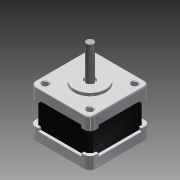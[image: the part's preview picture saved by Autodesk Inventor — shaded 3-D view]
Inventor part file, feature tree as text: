
AUTODESK INVENTOR PART (.ipt)
format: ipt  version: 2015 (Build 190159000, 159)  size: 244,736 bytes
history: native  units: mm
features: extrude x4, sketch x3, chamfer x2, pattern_circular x1, fillet x1, projected_geometry x1
ambient origin geometry x8: Origin, YZ Plane, XZ Plane, XY Plane, X Axis, Y Axis, Z Axis, Center Point
bodies: Solid1 (feature_tree)
feature tree (12):
  sketch  "Sketch1"  dims[d0=5.0mm d1=7.0mm]
  extrude  "Extrusion1"  Depth=7.0mm
  extrude  "Extrusion2"  Depth=42.0mm
  extrude  "Extrusion3"  Depth=1.0mm
  pattern_circular  "Circular Pattern1"  [2 undecoded]
  chamfer  "Chamfer1"  Distance=4.0mm
  extrude  "Extrusion4"  Depth=33.0mm TaperAngle=0.0deg
  chamfer  "Chamfer2"  Distance=2.0mm
  fillet  "Fillet1"  Radius=6.0mm
  sketch  "Sketch2"  dims[d2=22.0mm d3=42.0mm]
  sketch  "Sketch3"  dims[d4=4.0mm d5=31.0mm d6=31.0mm d7=4.0mm d8=33.0mm d9=0.0mm d10=2.0mm d11=0.0mm d12=6.0mm d13=7.0mm d14=2.0mm d15=2.0mm d16=0.0mm d17=40.0mm d18=360.0deg d20=2.0mm d21=2.0mm d22=45.0deg d23=58.0mm d24=0.0mm d25=0.5mm d26=2.0mm d27=45.0deg d28=1.0mm]
  projected_geometry  "Projected Loop4"
note: 2 required parameter values undecoded (feature->parameter linkage not recoverable at this tier; creation-order binding heuristic only, values carry confidence <= 0.55)
